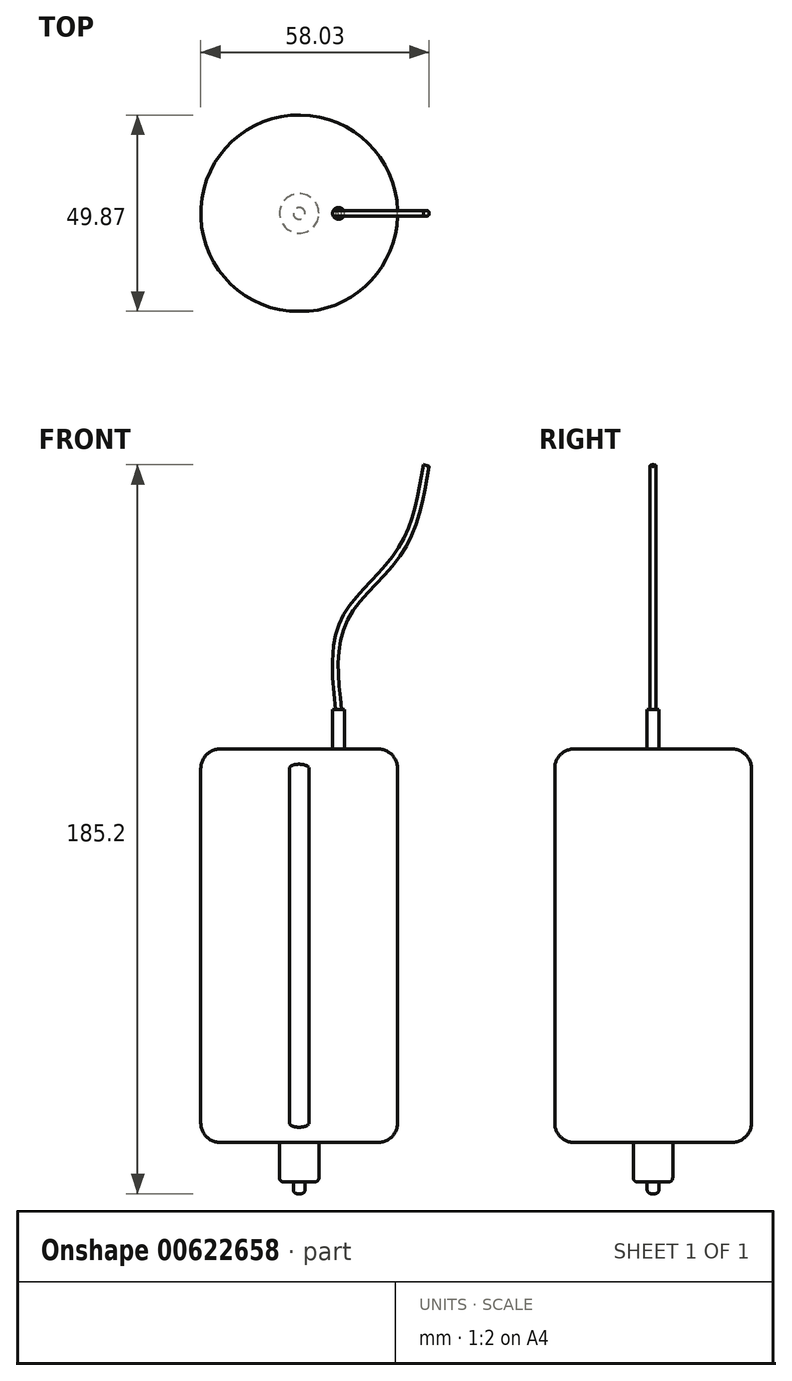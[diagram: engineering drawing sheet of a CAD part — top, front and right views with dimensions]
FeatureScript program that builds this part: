
annotation { "Feature Type Name" : "Feature", "Feature Type Description" : "" }
export const myFeature = defineFeature(function(context is Context, id is Id, definition is map)
    precondition{}
    {
        {
            var Q0;
            Q0=qCreatedBy(makeId("Top.planeOp"),FACE);
            var sketch = newSketch(context, id + "F0", { "sketchPlane" : qUnion([Q0])});
            skArc(sketch, "E0", {"start": v(2.5, -24.87) * mm, "mid": v(0, 25) * mm, "end": v(-2.5, -24.87) * mm});
            skLineSegment(sketch, "E1.bottom", {"start": v(2.5, -24.87) * mm, "end": v(-2.5, -24.87) * mm, "construction": true});
            skLineSegment(sketch, "E1.top", {"start": v(2.5, 24.87) * mm, "end": v(-2.5, 24.87) * mm, "construction": true});
            skLineSegment(sketch, "E1.left", {"start": v(2.5, -24.87) * mm, "end": v(2.5, 24.87) * mm, "construction": true});
            skLineSegment(sketch, "E1.right", {"start": v(-2.5, -24.87) * mm, "end": v(-2.5, 24.87) * mm, "construction": true});
            skLineSegment(sketch, "E2", {"start": v(-2.5, -24.87) * mm, "end": v(2.5, -24.87) * mm});
            skSolve(sketch);
        }
        {
            var Q0;
            Q0=makeQuery(id+"F0.imprint","IMPRINT",FACE,{"disambiguationData":[TD([[makeQuery(id+"F0.imprint","IMPRINT",EDGE,{"derivedFrom":sQuery(id+"F0.wireOp",EDGE,"E0")}),1.0]])]});
            extrude(context, id + "F1", {"entities" : qUnion([Q0]), "endBound" : BoundingType.SYMMETRIC, "depth" : 100 * mm, "offsetDistance" : 25 * mm});
        }
        {
            var Q0;
            Q0=makeQuery(id+"F1.opExtrude","CAP_FACE",FACE,{"disambiguationData":[OSD([sQuery(id+"F0.wireOp",EDGE,"E0")])],"isStart":true});
            var sketch = newSketch(context, id + "F2", { "sketchPlane" : qUnion([Q0])});
            skCircle(sketch, "E3", {"center": v(0, 0) * mm, "radius": 5 * mm});
            skSolve(sketch);
        }
        {
            var Q0;
            Q0=makeQuery(id+"F2.imprint","IMPRINT",FACE,{"disambiguationData":[TD([[makeQuery(id+"F2.imprint","IMPRINT",EDGE,{"derivedFrom":sQuery(id+"F2.wireOp",EDGE,"E3")}),1.0]])]});
            extrude(context, id + "F3", {"entities" : qUnion([Q0]), "operationType" : NewBodyOperationType.ADD, "depth" : 10 * mm, "offsetDistance" : 25 * mm});
        }
        {
            var Q0;
            Q0=makeQuery(id+"F3.opExtrude","CAP_FACE",FACE,{"disambiguationData":[OSD([sQuery(id+"F2.wireOp",EDGE,"E3")])],"isStart":false});
            var sketch = newSketch(context, id + "F4", { "sketchPlane" : qUnion([Q0])});
            skCircle(sketch, "E4", {"center": v(0, 0) * mm, "radius": 1.5 * mm});
            skSolve(sketch);
        }
        {
            var Q0;
            Q0=makeQuery(id+"F4.imprint","IMPRINT",FACE,{"disambiguationData":[TD([[makeQuery(id+"F4.imprint","IMPRINT",EDGE,{"derivedFrom":sQuery(id+"F4.wireOp",EDGE,"E4")}),1.0]])]});
            extrude(context, id + "F5", {"entities" : qUnion([Q0]), "operationType" : NewBodyOperationType.ADD, "depth" : 3 * mm, "offsetDistance" : 25 * mm});
        }
        {
            var Q0;
            Q0=makeQuery(id+"F1.opExtrude","CAP_FACE",FACE,{"disambiguationData":[OSD([sQuery(id+"F0.wireOp",EDGE,"E0")])],"isStart":false});
            var sketch = newSketch(context, id + "F6", { "sketchPlane" : qUnion([Q0])});
            skLineSegment(sketch, "E5", {"start": v(0, 0) * mm, "end": v(10, 0) * mm, "construction": true});
            skCircle(sketch, "E6", {"center": v(10, 0) * mm, "radius": 1.5 * mm});
            skSolve(sketch);
        }
        {
            var Q0;
            Q0 = qSketchRegion(id + "F6", true);
            extrude(context, id + "F7", {"entities" : qUnion([Q0]), "operationType" : NewBodyOperationType.ADD, "depth" : 10 * mm, "offsetDistance" : 25 * mm});
        }
        {
            var Q0;
            Q0=makeQuery(id+"F7.opExtrude","CAP_FACE",FACE,{"disambiguationData":[OSD([sQuery(id+"F6.wireOp",EDGE,"E6")])],"isStart":false});
            var sketch = newSketch(context, id + "F8", { "sketchPlane" : qUnion([Q0])});
            skCircle(sketch, "E7", {"center": v(10, 0) * mm, "radius": 0.75 * mm});
            skSolve(sketch);
        }
        {
            var Q0;
            Q0=qCreatedBy(makeId("Front.planeOp"),FACE);
            var sketch = newSketch(context, id + "F9", { "sketchPlane" : qUnion([Q0])});
            skFitSpline(sketch, "E8", {"points": [v(10, 60) * mm, v(11.11, 82.06) * mm, v(25.54, 100.24) * mm, v(32.3, 122) * mm], "startDerivative": vector(-7.03, 66.8) * mm, "endDerivative": vector(11.47, 67.9) * mm});
            skSolve(sketch);
        }
        {
            var Q0;
            Q0 = qSketchRegion(id + "F8", true);
            var Q1;
            Q1 = qConstructionFilter(qBodyType(qCreatedBy(id + "F9" ,EDGE), BodyType.WIRE), ConstructionObject.NO);
            sweep(context, id + "F10", {"operationType" : NewBodyOperationType.ADD, "profiles" : qUnion([Q0]), "path" : qUnion([Q1])});
        }
        {
            var Q0;
            Q0=makeQuery(id+"F1.opExtrude","CAP_EDGE",EDGE,{"disambiguationData":[OSD([sQuery(id+"F0.wireOp",EDGE,"E0")])],"isStart":true});
            var Q1;
            Q1=makeQuery(id+"F1.opExtrude","CAP_EDGE",EDGE,{"disambiguationData":[OSD([sQuery(id+"F0.wireOp",EDGE,"E0")])],"isStart":false});
            fillet(context, id + "F11", {"entities" : qUnion([Q0, Q1]), "radius" : 5 * mm, "tangentPropagation" : true, "allowEdgeOverflow" : false});
        }
        {
            var Q0;
            Q0=makeQuery(id+"F3.opExtrude","CAP_EDGE",EDGE,{"disambiguationData":[OSD([sQuery(id+"F2.wireOp",EDGE,"E3")])],"isStart":false});
            var Q1;
            Q1=makeQuery(id+"F5.opExtrude","CAP_EDGE",EDGE,{"disambiguationData":[OSD([sQuery(id+"F4.wireOp",EDGE,"E4")])],"isStart":false});
            fillet(context, id + "F12", {"entities" : qUnion([Q0, Q1]), "radius" : 1 * mm, "tangentPropagation" : true, "allowEdgeOverflow" : false});
        }
    });
